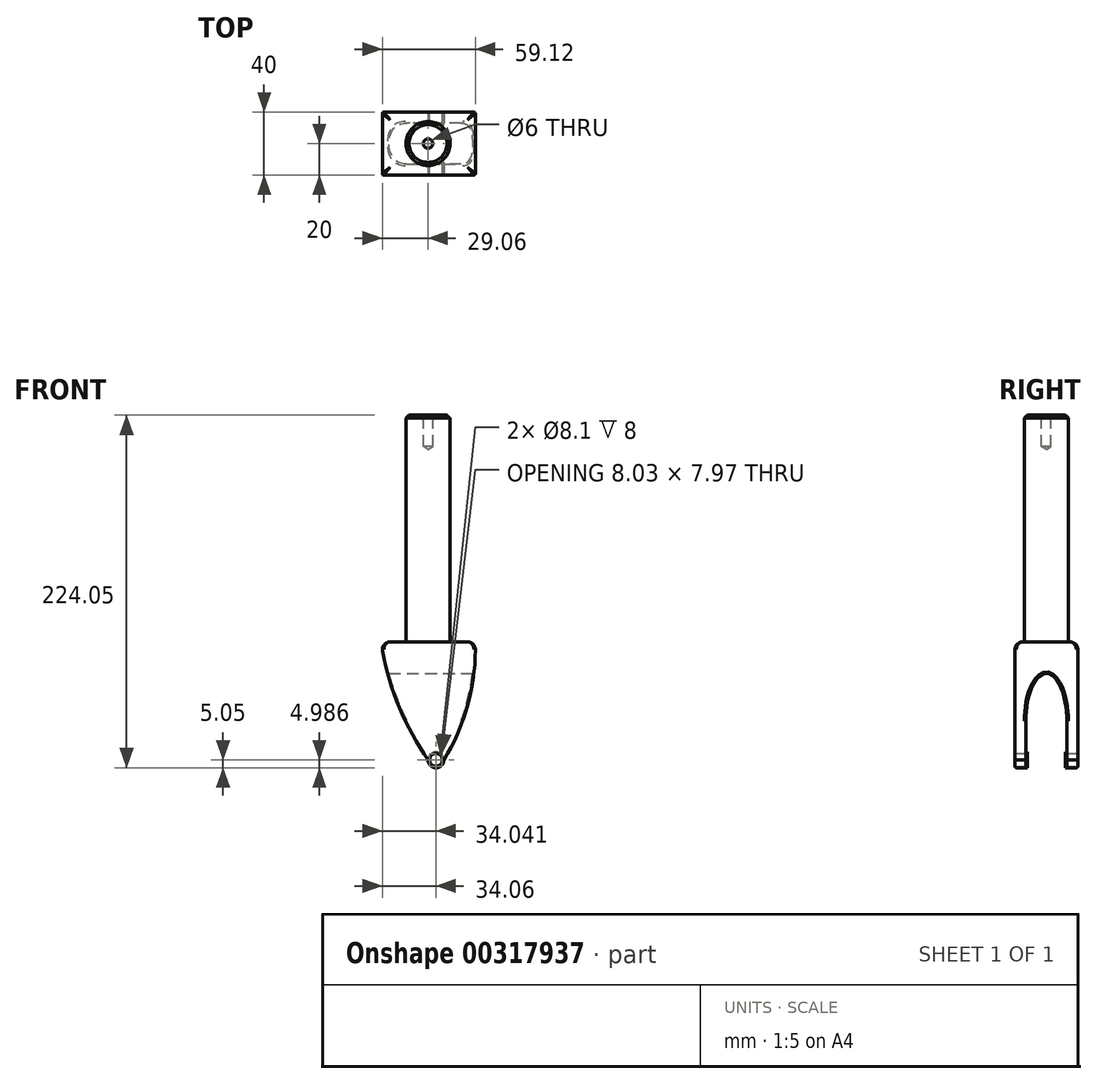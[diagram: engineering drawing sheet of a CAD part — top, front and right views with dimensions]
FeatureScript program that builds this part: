
annotation { "Feature Type Name" : "Feature", "Feature Type Description" : "" }
export const myFeature = defineFeature(function(context is Context, id is Id, definition is map)
    precondition{}
    {
        {
            var Q0;
            Q0=qCreatedBy(makeId("Top.planeOp"),FACE);
            var sketch = newSketch(context, id + "F0", { "sketchPlane" : qUnion([Q0])});
            skCircle(sketch, "E0", {"center": v(0, 0) * mm, "radius": 14 * mm});
            skSolve(sketch);
        }
        {
            var Q0;
            Q0=qSketchRegion(id+"F0",true);
            extrude(context, id + "F1", {"entities" : qUnion([Q0]), "depth" : 144 * mm});
        }
        {
            var Q0;
            Q0=qCreatedBy(makeId("Top.planeOp"),FACE);
            var sketch = newSketch(context, id + "F2", { "sketchPlane" : qUnion([Q0])});
            skLineSegment(sketch, "E1.bottom", {"start": v(40, -20) * mm, "end": v(-40, -20) * mm});
            skLineSegment(sketch, "E1.top", {"start": v(40, 20) * mm, "end": v(-40, 20) * mm});
            skLineSegment(sketch, "E1.left", {"start": v(40, -20) * mm, "end": v(40, 20) * mm});
            skLineSegment(sketch, "E1.right", {"start": v(-40, -20) * mm, "end": v(-40, 20) * mm});
            skPoint(sketch, "E1.middle", {"position": v(0, 0) * mm});
            skSolve(sketch);
        }
        {
            var Q0;
            Q0=qSketchRegion(id+"F2",true);
            extrude(context, id + "F3", {"entities" : qUnion([Q0]), "operationType" : NewBodyOperationType.ADD, "oppositeDirection" : true, "depth" : 80 * mm});
        }
        {
            var Q0;
            Q0=makeQuery(id+"F3.opExtrude","SWEPT_EDGE",EDGE,{"disambiguationData":[OSD([sQuery(id+"F2.wireOp",EDGE,"E1.bottom"),sQuery(id+"F2.wireOp",EDGE,"E1.left")])]});
            var Q1;
            Q1=makeQuery(id+"F3.opExtrude","SWEPT_EDGE",EDGE,{"disambiguationData":[OSD([sQuery(id+"F2.wireOp",EDGE,"E1.bottom"),sQuery(id+"F2.wireOp",EDGE,"E1.right")])]});
            var Q2;
            Q2=makeQuery(id+"F3.opExtrude","SWEPT_EDGE",EDGE,{"disambiguationData":[OSD([sQuery(id+"F2.wireOp",EDGE,"E1.top"),sQuery(id+"F2.wireOp",EDGE,"E1.right")])]});
            var Q3;
            Q3=makeQuery(id+"F3.opExtrude","SWEPT_EDGE",EDGE,{"disambiguationData":[OSD([sQuery(id+"F2.wireOp",EDGE,"E1.top"),sQuery(id+"F2.wireOp",EDGE,"E1.left")])]});
            fillet(context, id + "F4", {"entities" : qUnion([Q0, Q1, Q2, Q3]), "radius" : 5 * mm, "tangentPropagation" : true, "allowEdgeOverflow" : false});
        }
        {
            var Q0;
            Q0=qCreatedBy(makeId("Front.planeOp"),FACE);
            var sketch = newSketch(context, id + "F5", { "sketchPlane" : qUnion([Q0])});
            skPoint(sketch, "E2", {"position": v(-35.6, 0) * mm});
            skPoint(sketch, "E3", {"position": v(-30, 0) * mm});
            skLineSegment(sketch, "E4", {"start": v(-30, -90) * mm, "end": v(30, -90) * mm});
            skLineSegment(sketch, "E5", {"start": v(30, -8.37) * mm, "end": v(30, 0) * mm});
            skLineSegment(sketch, "E6", {"start": v(30, 0) * mm, "end": v(-30, 0) * mm});
            skPoint(sketch, "E7", {"position": v(5, -75) * mm});
            skArc(sketch, "E8", {"start": v(0, -75) * mm, "mid": v(5, -80) * mm, "end": v(10, -75) * mm});
            skLineSegment(sketch, "E9", {"start": v(10, -75) * mm, "end": v(0, -75) * mm});
            skArc(sketch, "E10", {"start": v(-30, 0) * mm, "mid": v(-19.26, -39.2) * mm, "end": v(0, -75) * mm});
            skArc(sketch, "E11", {"start": v(10, -75) * mm, "mid": v(25.5, -38.97) * mm, "end": v(30, 0) * mm});
            skLineSegment(sketch, "E12", {"start": v(30, 0) * mm, "end": v(43.9, 0) * mm});
            skLineSegment(sketch, "E13", {"start": v(43.9, 0) * mm, "end": v(41.1, -18.15) * mm});
            skLineSegment(sketch, "E14", {"start": v(-30, 0) * mm, "end": v(-45.43, 0) * mm});
            skLineSegment(sketch, "E15", {"start": v(-45.43, 0) * mm, "end": v(-66.81, -82.88) * mm});
            skLineSegment(sketch, "E16", {"start": v(-66.81, -82.88) * mm, "end": v(-30, -90) * mm});
            skLineSegment(sketch, "E17", {"start": v(41.1, -18.15) * mm, "end": v(46.7, -90.87) * mm});
            skLineSegment(sketch, "E18", {"start": v(46.7, -90.87) * mm, "end": v(30, -90) * mm});
            skSolve(sketch);
        }
        {
            var Q0;
            Q0=qCreatedBy(makeId("Right.planeOp"),FACE);
            var sketch = newSketch(context, id + "F6", { "sketchPlane" : qUnion([Q0])});
            skEllipticalArc(sketch, "E19", {});
            skLineSegment(sketch, "E20", {"start": v(13, -50) * mm, "end": v(13, -80) * mm});
            skLineSegment(sketch, "E21", {"start": v(13, -80) * mm, "end": v(-13, -80) * mm});
            skPoint(sketch, "E21.endSnap0", {"position": v(-13, -50) * mm});
            skLineSegment(sketch, "E22", {"start": v(-13, -80) * mm, "end": v(-13, -50) * mm});
            skPoint(sketch, "E23", {"position": v(0, -20) * mm});
            const initialGuessF6  = {"E19": [0, -0.05, 0, 1, 0.03, 0.013, 4.71238898038469, 1.5707963267948966]};
            skSetInitialGuess(sketch, initialGuessF6);
            skSolve(sketch);
        }
        {
            var Q0;
            Q0=makeQuery(id+"F5.imprint","IMPRINT",FACE,{"disambiguationData":[TD([[makeQuery(id+"F5.imprint","IMPRINT",EDGE,{"derivedFrom":sQuery(id+"F5.wireOp",EDGE,"E4")}),1.0]])]});
            extrude(context, id + "F7", {"entities" : qUnion([Q0]), "operationType" : NewBodyOperationType.REMOVE, "oppositeDirection" : true, "depth" : 4444 * mm, "hasSecondDirection" : true, "secondDirectionOppositeDirection" : false, "secondDirectionDepth" : 25 * mm});
        }
        {
            var Q0;
            Q0=qSketchRegion(id+"F6",true);
            extrude(context, id + "F8", {"entities" : qUnion([Q0]), "operationType" : NewBodyOperationType.REMOVE, "endBound" : BoundingType.SYMMETRIC, "depth" : 70 * mm});
        }
        {
            var Q0;
            Q0=makeQuery(id+"F3.opExtrude","SWEPT_FACE",FACE,{"disambiguationData":[OSD([sQuery(id+"F2.wireOp",EDGE,"E1.top")])]});
            var sketch = newSketch(context, id + "F9", { "sketchPlane" : qUnion([Q0])});
            skPoint(sketch, "E24", {"position": v(-5, -75) * mm});
            skSolve(sketch);
        }
        {
            var Q0;
            Q0=sQuery(id+"F9.wireOp",VERTEX,"E24");
            var Q1;
            Q1=makeQuery(id+"F1.opExtrude","SWEPT_BODY",BODY,{"disambiguationData":[OSD([sQuery(id+"F0.wireOp",EDGE,"E0")])]});
            hole(context, id + "F10", {"style" : HoleStyle.SIMPLE, "endStyle" : HoleEndStyle.THROUGH, "holeDiameter" : 8.1 * mm, "locations" : qUnion([Q0]), "scope" : qUnion([Q1]), "isTappedThrough" : true});
        }
        {
            var Q0;
            Q0=makeQuery(id+"F8.boolean.opBoolean","COPY",FACE,{"derivedFrom":makeQuery(id+"F8.opExtrude","SWEPT_FACE",FACE,{"disambiguationData":[OSD([sQuery(id+"F6.wireOp",EDGE,"E22")])]})});
            var sketch = newSketch(context, id + "F11", { "sketchPlane" : qUnion([Q0])});
            skCircle(sketch, "E25.0", {"center": v(-5, -75) * mm, "radius": 4.05 * mm});
            skCircle(sketch, "E26.0", {"center": v(-5, -75) * mm, "radius": 5.05 * mm});
            skSolve(sketch);
        }
        {
            var Q0;
            Q0=qSketchRegion(id+"F11",true);
            extrude(context, id + "F12", {"entities" : qUnion([Q0]), "depth" : 1 * mm});
        }
        {
            var Q0;
            Q0=makeQuery(id+"F12.opExtrude","SWEPT_BODY",BODY,{"disambiguationData":[OSD([sQuery(id+"F11.wireOp",EDGE,"E25.0"),sQuery(id+"F11.wireOp",EDGE,"E26.0")])]});
            var Q1;
            Q1=qCreatedBy(makeId("Front.planeOp"),FACE);
            mirror(context, id + "F13", {"operationType" : NewBodyOperationType.ADD, "entities" : qUnion([Q0]), "mirrorPlane" : qUnion([Q1])});
        }
        {
            var Q0;
            Q0=makeQuery(id+"F1.opExtrude","CAP_FACE",FACE,{"disambiguationData":[OSD([sQuery(id+"F0.wireOp",EDGE,"E0")])],"isStart":false});
            var sketch = newSketch(context, id + "F14", { "sketchPlane" : qUnion([Q0])});
            skPoint(sketch, "E27", {"position": v(0, 0) * mm});
            skSolve(sketch);
        }
        {
            var Q0;
            Q0=sQuery(id+"F14.wireOp",VERTEX,"E27");
            var Q1;
            Q1=makeQuery(id+"F1.opExtrude","SWEPT_BODY",BODY,{"disambiguationData":[OSD([sQuery(id+"F0.wireOp",EDGE,"E0")])]});
            hole(context, id + "F15", {"style" : HoleStyle.SIMPLE, "endStyle" : HoleEndStyle.BLIND, "holeDiameter" : 6 * mm, "holeDepth" : 20 * mm, "locations" : qUnion([Q0]), "scope" : qUnion([Q1])});
        }
        {
            var Q0;
            Q0=makeQuery(id+"F1.opExtrude","CAP_EDGE",EDGE,{"disambiguationData":[OSD([sQuery(id+"F0.wireOp",EDGE,"E0")])],"isStart":false});
            chamfer(context, id + "F16", {"entities" : qUnion([Q0]), "width" : 2 * mm, "tangentPropagation" : true});
        }
        {
            var Q0;
            Q0=makeQuery(id+"F8.boolean.opBoolean","INTERSECT",EDGE,{"derivedFrom":[makeQuery(id+"F7.boolean.opBoolean","COPY",FACE,{"derivedFrom":makeQuery(id+"F7.opExtrude","SWEPT_FACE",FACE,{"disambiguationData":[OSD([sQuery(id+"F5.wireOp",EDGE,"E11")])]})}),makeQuery(id+"F8.opExtrude","SWEPT_FACE",FACE,{"disambiguationData":[OSD([sQuery(id+"F6.wireOp",EDGE,"E19")])]})]});
            var Q1;
            {var subQ1=makeQuery(id+"F8.opExtrude","SWEPT_FACE",FACE,{"disambiguationData":[OSD([sQuery(id+"F6.wireOp",EDGE,"E22")])]});var subQ2=makeQuery(id+"F7.boolean.opBoolean","COPY",FACE,{"derivedFrom":makeQuery(id+"F7.opExtrude","SWEPT_FACE",FACE,{"disambiguationData":[OSD([sQuery(id+"F5.wireOp",EDGE,"E11")])]})});Q1=makeQuery(id+"F13.boolean.opBoolean","SPLIT",EDGE,{"disambiguationData":[TD([makeQuery(id+"F8.boolean.opBoolean","COPY",FACE,{"derivedFrom":makeQuery(id+"F8.opExtrude","SWEPT_FACE",FACE,{"disambiguationData":[OSD([sQuery(id+"F6.wireOp",EDGE,"E19")])]})})])],"derivedFrom":makeQuery(id+"F8.boolean.opBoolean","INTERSECT",EDGE,{"derivedFrom":[subQ2,subQ1]})});}
            var Q2;
            Q2=makeQuery(id+"F7.boolean.opBoolean","INTERSECT",EDGE,{"derivedFrom":[makeQuery(id+"F3.opExtrude","SWEPT_FACE",FACE,{"disambiguationData":[OSD([sQuery(id+"F2.wireOp",EDGE,"E1.bottom")])]}),makeQuery(id+"F7.opExtrude","SWEPT_FACE",FACE,{"disambiguationData":[OSD([sQuery(id+"F5.wireOp",EDGE,"E11")])]})]});
            var Q3;
            Q3=makeQuery(id+"F7.boolean.opBoolean","INTERSECT",EDGE,{"derivedFrom":[makeQuery(id+"F3.opExtrude","SWEPT_FACE",FACE,{"disambiguationData":[OSD([sQuery(id+"F2.wireOp",EDGE,"E1.top")])]}),makeQuery(id+"F7.opExtrude","SWEPT_FACE",FACE,{"disambiguationData":[OSD([sQuery(id+"F5.wireOp",EDGE,"E11")])]})]});
            var Q4;
            {var subQ1=makeQuery(id+"F8.opExtrude","SWEPT_FACE",FACE,{"disambiguationData":[OSD([sQuery(id+"F6.wireOp",EDGE,"E20")])]});var subQ2=makeQuery(id+"F7.boolean.opBoolean","COPY",FACE,{"derivedFrom":makeQuery(id+"F7.opExtrude","SWEPT_FACE",FACE,{"disambiguationData":[OSD([sQuery(id+"F5.wireOp",EDGE,"E11")])]})});Q4=makeQuery(id+"F13.boolean.opBoolean","SPLIT",EDGE,{"disambiguationData":[TD([makeQuery(id+"F8.boolean.opBoolean","COPY",FACE,{"derivedFrom":makeQuery(id+"F8.opExtrude","SWEPT_FACE",FACE,{"disambiguationData":[OSD([sQuery(id+"F6.wireOp",EDGE,"E19")])]})})])],"derivedFrom":makeQuery(id+"F8.boolean.opBoolean","INTERSECT",EDGE,{"derivedFrom":[subQ2,subQ1]})});}
            var Q5;
            Q5=makeQuery(id+"F7.boolean.opBoolean","INTERSECT",EDGE,{"derivedFrom":[makeQuery(id+"F3.opExtrude","SWEPT_FACE",FACE,{"disambiguationData":[OSD([sQuery(id+"F2.wireOp",EDGE,"E1.bottom")])]}),makeQuery(id+"F7.opExtrude","SWEPT_FACE",FACE,{"disambiguationData":[OSD([sQuery(id+"F5.wireOp",EDGE,"E10")])]})]});
            var Q6;
            Q6=makeQuery(id+"F7.boolean.opBoolean","INTERSECT",EDGE,{"derivedFrom":[makeQuery(id+"F3.opExtrude","SWEPT_FACE",FACE,{"disambiguationData":[OSD([sQuery(id+"F2.wireOp",EDGE,"E1.bottom")])]}),makeQuery(id+"F7.opExtrude","SWEPT_FACE",FACE,{"disambiguationData":[OSD([sQuery(id+"F5.wireOp",EDGE,"E8")])]})]});
            var Q7;
            Q7=makeQuery(id+"F7.boolean.opBoolean","INTERSECT",EDGE,{"derivedFrom":[makeQuery(id+"F3.opExtrude","SWEPT_FACE",FACE,{"disambiguationData":[OSD([sQuery(id+"F2.wireOp",EDGE,"E1.top")])]}),makeQuery(id+"F7.opExtrude","SWEPT_FACE",FACE,{"disambiguationData":[OSD([sQuery(id+"F5.wireOp",EDGE,"E8")])]})]});
            var Q8;
            Q8=makeQuery(id+"F7.boolean.opBoolean","INTERSECT",EDGE,{"derivedFrom":[makeQuery(id+"F3.opExtrude","SWEPT_FACE",FACE,{"disambiguationData":[OSD([sQuery(id+"F2.wireOp",EDGE,"E1.top")])]}),makeQuery(id+"F7.opExtrude","SWEPT_FACE",FACE,{"disambiguationData":[OSD([sQuery(id+"F5.wireOp",EDGE,"E10")])]})]});
            var Q9;
            Q9=makeQuery(id+"F8.boolean.opBoolean","INTERSECT",EDGE,{"derivedFrom":[makeQuery(id+"F7.boolean.opBoolean","COPY",FACE,{"derivedFrom":makeQuery(id+"F7.opExtrude","SWEPT_FACE",FACE,{"disambiguationData":[OSD([sQuery(id+"F5.wireOp",EDGE,"E10")])]})}),makeQuery(id+"F8.opExtrude","SWEPT_FACE",FACE,{"disambiguationData":[OSD([sQuery(id+"F6.wireOp",EDGE,"E19")])]})]});
            var Q10;
            {var subQ1=makeQuery(id+"F8.opExtrude","SWEPT_FACE",FACE,{"disambiguationData":[OSD([sQuery(id+"F6.wireOp",EDGE,"E20")])]});var subQ2=makeQuery(id+"F7.boolean.opBoolean","COPY",FACE,{"derivedFrom":makeQuery(id+"F7.opExtrude","SWEPT_FACE",FACE,{"disambiguationData":[OSD([sQuery(id+"F5.wireOp",EDGE,"E10")])]})});Q10=makeQuery(id+"F13.boolean.opBoolean","SPLIT",EDGE,{"disambiguationData":[TD([makeQuery(id+"F8.boolean.opBoolean","COPY",FACE,{"derivedFrom":makeQuery(id+"F8.opExtrude","SWEPT_FACE",FACE,{"disambiguationData":[OSD([sQuery(id+"F6.wireOp",EDGE,"E19")])]})})])],"derivedFrom":makeQuery(id+"F8.boolean.opBoolean","INTERSECT",EDGE,{"derivedFrom":[subQ2,subQ1]})});}
            var Q11;
            {var subQ1=makeQuery(id+"F8.opExtrude","SWEPT_FACE",FACE,{"disambiguationData":[OSD([sQuery(id+"F6.wireOp",EDGE,"E22")])]});var subQ2=makeQuery(id+"F7.boolean.opBoolean","COPY",FACE,{"derivedFrom":makeQuery(id+"F7.opExtrude","SWEPT_FACE",FACE,{"disambiguationData":[OSD([sQuery(id+"F5.wireOp",EDGE,"E10")])]})});Q11=makeQuery(id+"F13.boolean.opBoolean","SPLIT",EDGE,{"disambiguationData":[TD([makeQuery(id+"F8.boolean.opBoolean","COPY",FACE,{"derivedFrom":makeQuery(id+"F8.opExtrude","SWEPT_FACE",FACE,{"disambiguationData":[OSD([sQuery(id+"F6.wireOp",EDGE,"E19")])]})})])],"derivedFrom":makeQuery(id+"F8.boolean.opBoolean","INTERSECT",EDGE,{"derivedFrom":[subQ2,subQ1]})});}
            fillet(context, id + "F17", {"entities" : qUnion([Q0, Q1, Q2, Q3, Q4, Q5, Q6, Q7, Q8, Q9, Q10, Q11]), "radius" : 1 * mm, "tangentPropagation" : true, "allowEdgeOverflow" : false});
        }
        {
            var Q0;
            Q0=makeQuery(id+"F3.opExtrude","CAP_EDGE",EDGE,{"disambiguationData":[OSD([sQuery(id+"F2.wireOp",EDGE,"E1.bottom")])],"isStart":true});
            var Q1;
            Q1=makeQuery(id+"F7.boolean.opBoolean","COPY",EDGE,{"derivedFrom":makeQuery(id+"F7.opExtrude","SWEPT_EDGE",EDGE,{"disambiguationData":[OSD([sQuery(id+"F5.wireOp",EDGE,"E5"),sQuery(id+"F5.wireOp",EDGE,"E6"),sQuery(id+"F5.wireOp",EDGE,"E11"),sQuery(id+"F5.wireOp",EDGE,"E12")])]})});
            var Q2;
            Q2=makeQuery(id+"F3.opExtrude","CAP_EDGE",EDGE,{"disambiguationData":[OSD([sQuery(id+"F2.wireOp",EDGE,"E1.top")])],"isStart":true});
            var Q3;
            Q3=makeQuery(id+"F7.boolean.opBoolean","COPY",EDGE,{"derivedFrom":makeQuery(id+"F7.opExtrude","SWEPT_EDGE",EDGE,{"disambiguationData":[OSD([sQuery(id+"F5.wireOp",EDGE,"E6"),sQuery(id+"F5.wireOp",EDGE,"E10"),sQuery(id+"F5.wireOp",EDGE,"E14")])]})});
            fillet(context, id + "F18", {"entities" : qUnion([Q0, Q1, Q2, Q3]), "radius" : 5 * mm, "tangentPropagation" : true, "allowEdgeOverflow" : false});
        }
    });
